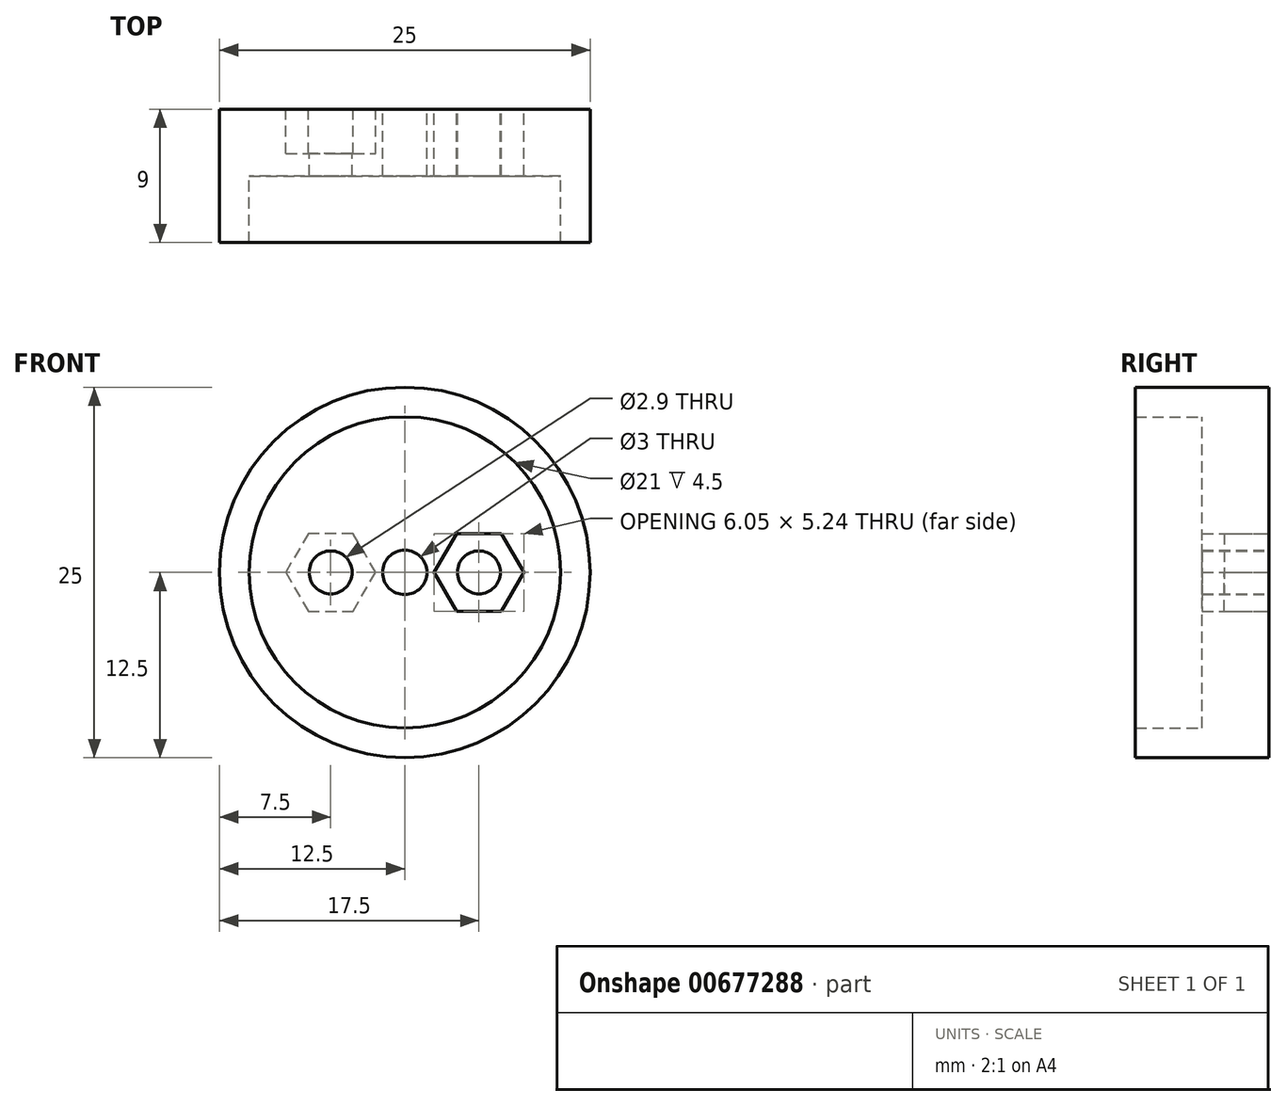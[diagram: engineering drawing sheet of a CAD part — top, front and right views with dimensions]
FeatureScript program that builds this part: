
annotation { "Feature Type Name" : "Feature", "Feature Type Description" : "" }
export const myFeature = defineFeature(function(context is Context, id is Id, definition is map)
    precondition{}
    {
        {
            var Q0;
            Q0=qCreatedBy(makeId("Front.planeOp"),FACE);
            var sketch = newSketch(context, id + "F0", { "sketchPlane" : qUnion([Q0])});
            skCircle(sketch, "E0", {"center": v(0, 0) * mm, "radius": 10.5 * mm});
            skCircle(sketch, "E1", {"center": v(0, 0) * mm, "radius": 12.5 * mm});
            skCircle(sketch, "E2", {"center": v(0, 0) * mm, "radius": 1.5 * mm});
            skSolve(sketch);
        }
        {
            var Q0;
            Q0=makeQuery(id+"F0.imprint","IMPRINT",FACE,{"disambiguationData":[TD([[makeQuery(id+"F0.imprint","IMPRINT",EDGE,{"derivedFrom":sQuery(id+"F0.wireOp",EDGE,"E0")}),1.0]])]});
            extrude(context, id + "F1", {"entities" : qUnion([Q0]), "depth" : 4.5 * mm, "offsetDistance" : 25 * mm});
        }
        {
            var Q0;
            Q0 = qSketchRegion(id + "F0", true);
            extrude(context, id + "F2", {"entities" : qUnion([Q0]), "operationType" : NewBodyOperationType.ADD, "depth" : 9 * mm, "offsetDistance" : 25 * mm});
        }
        {
            var Q0;
            {var subQ0=sQuery(id+"F0.wireOp",EDGE,"E0");Q0=makeQuery(id+"F2.boolean.opBoolean","MERGE",FACE,{"derivedFrom":[makeQuery(id+"F1.opExtrude","CAP_FACE",FACE,{"disambiguationData":[OSD([subQ0,sQuery(id+"F0.wireOp",EDGE,"E2")])],"isStart":true}),makeQuery(id+"F2.opExtrude","CAP_FACE",FACE,{"disambiguationData":[OSD([subQ0,sQuery(id+"F0.wireOp",EDGE,"E1")])],"isStart":true})]});}
            var sketch = newSketch(context, id + "F3", { "sketchPlane" : qUnion([Q0])});
            skLineSegment(sketch, "E3", {"start": v(0, 0) * mm, "end": v(5, 0) * mm});
            skCircle(sketch, "E4.cCircle", {"center": v(5, 0) * mm, "radius": 2.62 * mm, "construction": true});
            skLineSegment(sketch, "E4.0", {"start": v(6.51, -2.62) * mm, "end": v(3.49, -2.62) * mm});
            skLineSegment(sketch, "E4.1", {"start": v(3.49, -2.62) * mm, "end": v(1.97, 0) * mm});
            skLineSegment(sketch, "E4.2", {"start": v(1.98, 0) * mm, "end": v(3.49, 2.62) * mm});
            skLineSegment(sketch, "E4.3", {"start": v(3.49, 2.62) * mm, "end": v(6.51, 2.62) * mm});
            skLineSegment(sketch, "E4.4", {"start": v(6.51, 2.62) * mm, "end": v(8.03, 0) * mm});
            skLineSegment(sketch, "E4.5", {"start": v(8.02, 0) * mm, "end": v(6.51, -2.62) * mm});
            skPoint(sketch, "E4.0.midPoint", {"position": v(5, -2.62) * mm});
            skCircle(sketch, "E5", {"center": v(5, 0) * mm, "radius": 1.45 * mm});
            skLineSegment(sketch, "E6.MirrorCS", {"start": v(-3.49, 2.62) * mm, "end": v(-6.51, 2.62) * mm});
            skLineSegment(sketch, "E7.MirrorCS", {"start": v(-1.98, 0) * mm, "end": v(-3.49, 2.62) * mm});
            skLineSegment(sketch, "E8.MirrorCS", {"start": v(-3.49, -2.62) * mm, "end": v(-1.97, 0) * mm});
            skLineSegment(sketch, "E9.MirrorCS", {"start": v(-6.51, -2.62) * mm, "end": v(-3.49, -2.62) * mm});
            skLineSegment(sketch, "E10.MirrorCS", {"start": v(-8.02, 0) * mm, "end": v(-6.51, -2.62) * mm});
            skLineSegment(sketch, "E11.MirrorCS", {"start": v(-6.51, 2.62) * mm, "end": v(-8.03, 0) * mm});
            skCircle(sketch, "E12.MirrorC", {"center": v(-5, 0) * mm, "radius": 2.62 * mm, "construction": true});
            skCircle(sketch, "E13.MirrorC", {"center": v(-5, 0) * mm, "radius": 1.45 * mm});
            skSolve(sketch);
        }
        {
            var Q0;
            Q0=makeQuery(id+"F3.imprint","IMPRINT",FACE,{"disambiguationData":[TD([[makeQuery(id+"F3.imprint","IMPRINT",EDGE,{"derivedFrom":sQuery(id+"F3.wireOp",EDGE,"E5")}),1.0]])]});
            extrude(context, id + "F4", {"entities" : qUnion([Q0]), "operationType" : NewBodyOperationType.REMOVE, "oppositeDirection" : true, "depth" : 4.5 * mm, "offsetDistance" : 25 * mm});
        }
        {
            var Q0;
            Q0=makeQuery(id+"F3.imprint","IMPRINT",FACE,{"disambiguationData":[TD([[makeQuery(id+"F3.imprint","IMPRINT",EDGE,{"derivedFrom":sQuery(id+"F3.wireOp",EDGE,"E13.MirrorC")}),-1.0]])]});
            extrude(context, id + "F5", {"entities" : qUnion([Q0]), "operationType" : NewBodyOperationType.REMOVE, "oppositeDirection" : true, "depth" : 4.5 * mm, "offsetDistance" : 25 * mm});
        }
        {
            var Q0;
            Q0=makeQuery(id+"F3.imprint","IMPRINT",FACE,{"disambiguationData":[TD([[makeQuery(id+"F3.imprint","IMPRINT",EDGE,{"derivedFrom":sQuery(id+"F3.wireOp",EDGE,"E6.MirrorCS")}),1.0]])]});
            var Q1;
            Q1=makeQuery(id+"F3.imprint","IMPRINT",FACE,{"disambiguationData":[TD([[makeQuery(id+"F3.imprint","IMPRINT",EDGE,{"derivedFrom":sQuery(id+"F3.wireOp",EDGE,"E4.0")}),-1.0]])]});
            extrude(context, id + "F6", {"entities" : qUnion([Q0, Q1]), "operationType" : NewBodyOperationType.REMOVE, "oppositeDirection" : true, "depth" : 3 * mm, "offsetDistance" : 25 * mm});
        }
    });
